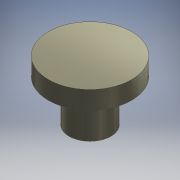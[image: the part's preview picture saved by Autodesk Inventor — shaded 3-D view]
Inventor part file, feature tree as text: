
AUTODESK INVENTOR PART (.ipt)
format: ipt  version: 2016 (Build 200138000, 138)  size: 96,768 bytes
history: native  units: mm
features: extrude x2, other x1, sketch x1
ambient origin geometry x8: Origin, YZ Plane, XZ Plane, XY Plane, X Axis, Y Axis, Z Axis, Center Point
bodies: Body1 (feature_tree)
feature tree (4):
  other  "ソリッド1"
  sketch  "スケッチ1"
  extrude  "押し出し1"  Depth=6.0mm
  extrude  "押し出し2"  Depth=3.0mm
